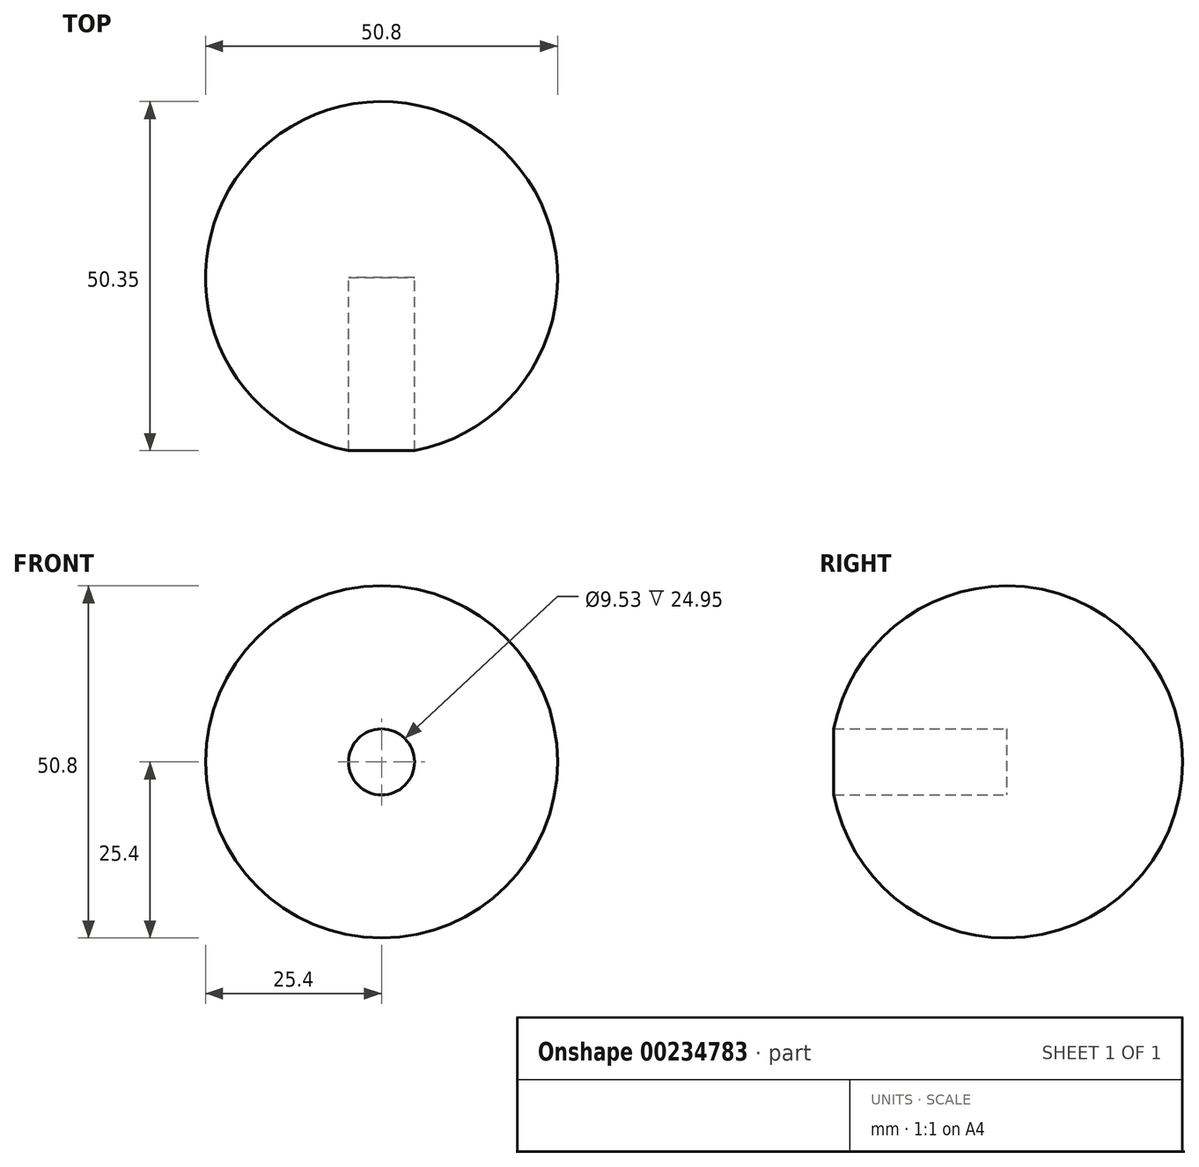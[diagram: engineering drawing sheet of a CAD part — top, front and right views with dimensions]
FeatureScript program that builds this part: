
annotation { "Feature Type Name" : "Feature", "Feature Type Description" : "" }
export const myFeature = defineFeature(function(context is Context, id is Id, definition is map)
    precondition{}
    {
        {
            var Q0;
            Q0=qCreatedBy(makeId("Front.planeOp"),FACE);
            var sketch = newSketch(context, id + "F0", { "sketchPlane" : qUnion([Q0])});
            skArc(sketch, "E0", {"start": v(0, 25.4) * mm, "mid": v(-25.4, 0) * mm, "end": v(0, -25.4) * mm});
            skLineSegment(sketch, "E1", {"start": v(0, 25.4) * mm, "end": v(0, -25.4) * mm});
            skSolve(sketch);
        }
        {
            var Q0;
            {var subQ0=sQuery(id+"F0.wireOp",EDGE,"E0");Q0=makeQuery(id+"F0.imprint","IMPRINT",FACE,{"disambiguationData":[TD([[makeQuery(id+"F0.imprint","IMPRINT",EDGE,{"derivedFrom":subQ0}),1.0]])]});}
            var Q1;
            {var subQ0=sQuery(id+"F0.wireOp",EDGE,"7f40c8ae-ebcd-4a4f-9072-71cebebe32c6");var subQ1=sQuery(id+"F0.wireOp",EDGE,"E1");var subQ2=makeQuery(id+"F0.imprint","INTERSECT",VERTEX,{"disambiguationData":[OD(0.0)],"derivedFrom":[subQ1,subQ0]});Q1=makeQuery(id+"F0.imprint","IMPRINT",FACE,{"disambiguationData":[TD([[makeQuery(id+"F0.imprint","IMPRINT",EDGE,{"disambiguationData":[TD([[subQ2,-1.0]])],"derivedFrom":subQ1}),-1.0]])]});}
            var Q2;
            Q2=sQuery(id+"F0.wireOp",EDGE,"E1");
            revolve(context, id + "F1", {"entities" : qUnion([Q0, Q1]), "axis" : qUnion([Q2]), "revolveType" : RevolveType.FULL});
        }
        {
            var Q0;
            Q0=sQuery(id+"F0.wireOp",VERTEX,"E0.center");
            var Q1;
            Q1=makeQuery(id+"F1.opRevolve","SWEPT_BODY",BODY,{"disambiguationData":[OSD([sQuery(id+"F0.wireOp",EDGE,"E0"),sQuery(id+"F0.wireOp",EDGE,"E1")])]});
            hole(context, id + "F2", {"style" : HoleStyle.SIMPLE, "endStyle" : HoleEndStyle.THROUGH, "oppositeDirection" : true, "holeDiameter" : 9.52 * mm, "locations" : qUnion([Q0]), "scope" : qUnion([Q1]), "isTappedThrough" : true});
        }
    });
